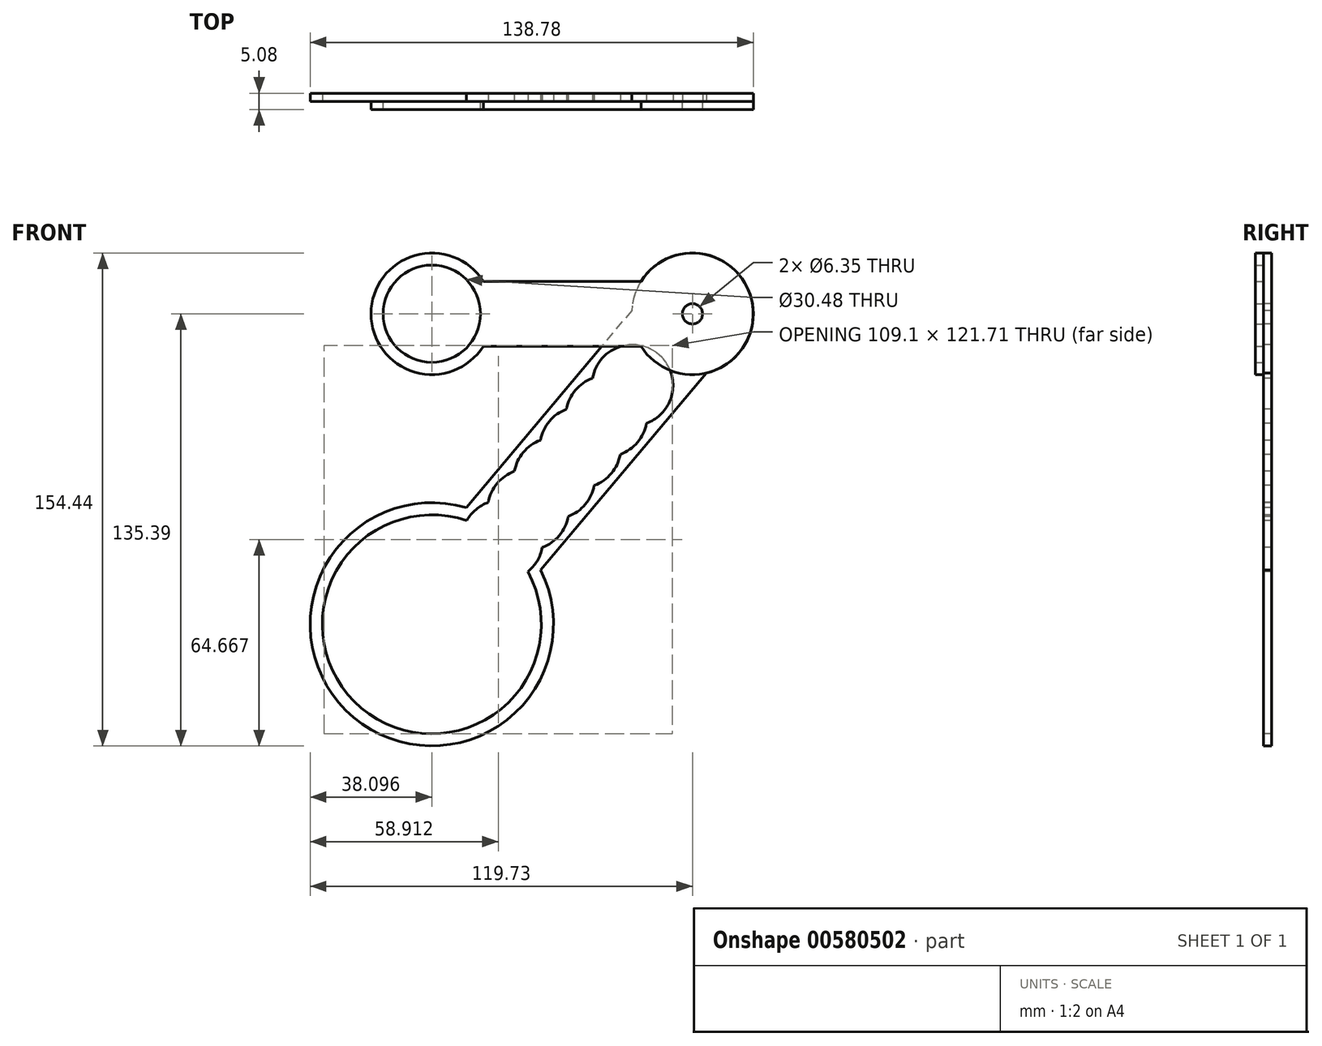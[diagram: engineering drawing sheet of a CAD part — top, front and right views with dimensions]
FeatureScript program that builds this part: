
annotation { "Feature Type Name" : "Feature", "Feature Type Description" : "" }
export const myFeature = defineFeature(function(context is Context, id is Id, definition is map)
    precondition{}
    {
        {
            var Q0;
            Q0=qCreatedBy(makeId("Front.planeOp"),FACE);
            var sketch = newSketch(context, id + "F0", { "sketchPlane" : qUnion([Q0])});
            skCircle(sketch, "E0", {"center": v(-81.63, 0) * mm, "radius": 19.05 * mm});
            skCircle(sketch, "E1", {"center": v(0, 0) * mm, "radius": 19.05 * mm});
            skCircle(sketch, "E2", {"center": v(-81.63, -97.29) * mm, "radius": 38.1 * mm});
            skLineSegment(sketch, "E3", {"start": v(-65.52, 10.16) * mm, "end": v(-16.11, 10.16) * mm});
            skLineSegment(sketch, "E4", {"start": v(4.33, -18.55) * mm, "end": v(-47.51, -80.33) * mm});
            skLineSegment(sketch, "E5", {"start": v(0, 0) * mm, "end": v(-81.63, 0) * mm, "construction": true});
            skLineSegment(sketch, "E6", {"start": v(0, 0) * mm, "end": v(-81.63, -97.29) * mm, "construction": true});
            skLineSegment(sketch, "E7.MirrorCS", {"start": v(-65.52, -10.16) * mm, "end": v(-16.11, -10.16) * mm});
            skLineSegment(sketch, "E8.MirrorCS", {"start": v(-19.02, 1.04) * mm, "end": v(-70.86, -60.74) * mm});
            skCircle(sketch, "E9", {"center": v(0, 0) * mm, "radius": 3.18 * mm});
            skCircle(sketch, "E10", {"center": v(-81.63, 0) * mm, "radius": 15.24 * mm});
            skCircle(sketch, "E11", {"center": v(-81.63, -97.29) * mm, "radius": 34.3 * mm});
            skCircle(sketch, "E12", {"center": v(-59.6, -71.02) * mm, "radius": 12.7 * mm});
            skCircle(sketch, "E13", {"center": v(-51.43, -61.3) * mm, "radius": 12.7 * mm});
            skCircle(sketch, "E14", {"center": v(-43.27, -51.56) * mm, "radius": 12.7 * mm});
            skCircle(sketch, "E15", {"center": v(-35.1, -41.83) * mm, "radius": 12.7 * mm});
            skCircle(sketch, "E16", {"center": v(-26.94, -32.1) * mm, "radius": 12.7 * mm});
            skCircle(sketch, "E17", {"center": v(-18.78, -22.38) * mm, "radius": 12.7 * mm});
            skSolve(sketch);
        }
        {
            var Q0;
            {var subQ0=sQuery(id+"F0.wireOp",EDGE,"E0");var subQ1=makeQuery(id+"F0.imprint","INTERSECT",VERTEX,{"derivedFrom":[subQ0,sQuery(id+"F0.wireOp",EDGE,"E3")]});Q0=makeQuery(id+"F0.imprint","IMPRINT",FACE,{"disambiguationData":[TD([[makeQuery(id+"F0.imprint","IMPRINT",EDGE,{"disambiguationData":[TD([[subQ1,-1.0]])],"derivedFrom":subQ0}),1.0]])]});}
            var Q1;
            {var subQ5=sQuery(id+"F0.wireOp",EDGE,"E3");Q1=makeQuery(id+"F0.imprint","IMPRINT",FACE,{"disambiguationData":[TD([[makeQuery(id+"F0.imprint","IMPRINT",EDGE,{"derivedFrom":subQ5}),-1.0]])]});}
            var Q2;
            {var subQ0=sQuery(id+"F0.wireOp",EDGE,"E1");var subQ1=makeQuery(id+"F0.imprint","INTERSECT",VERTEX,{"derivedFrom":[subQ0,sQuery(id+"F0.wireOp",EDGE,"E3")]});Q2=makeQuery(id+"F0.imprint","IMPRINT",FACE,{"disambiguationData":[TD([[makeQuery(id+"F0.imprint","IMPRINT",EDGE,{"disambiguationData":[TD([[subQ1,-1.0]])],"derivedFrom":subQ0}),1.0]])]});}
            var Q3;
            {var subQ0=sQuery(id+"F0.wireOp",EDGE,"E7.MirrorCS");var subQ1=sQuery(id+"F0.wireOp",EDGE,"E1");var subQ2=makeQuery(id+"F0.imprint","INTERSECT",VERTEX,{"derivedFrom":[subQ1,subQ0]});Q3=makeQuery(id+"F0.imprint","IMPRINT",FACE,{"disambiguationData":[TD([[makeQuery(id+"F0.imprint","IMPRINT",EDGE,{"disambiguationData":[TD([[subQ2,1.0]])],"derivedFrom":subQ1}),-1.0]])]});}
            var Q4;
            {var subQ0=sQuery(id+"F0.wireOp",EDGE,"E8.MirrorCS");var subQ1=sQuery(id+"F0.wireOp",EDGE,"E1");var subQ2=makeQuery(id+"F0.imprint","INTERSECT",VERTEX,{"derivedFrom":[subQ1,subQ0]});Q4=makeQuery(id+"F0.imprint","IMPRINT",FACE,{"disambiguationData":[TD([[makeQuery(id+"F0.imprint","IMPRINT",EDGE,{"disambiguationData":[TD([[subQ2,-1.0]])],"derivedFrom":subQ1}),-1.0]])]});}
            var Q5;
            {var subQ0=sQuery(id+"F0.wireOp",EDGE,"E1");var subQ1=makeQuery(id+"F0.imprint","INTERSECT",VERTEX,{"derivedFrom":[subQ0,sQuery(id+"F0.wireOp",EDGE,"E7.MirrorCS")]});Q5=makeQuery(id+"F0.imprint","IMPRINT",FACE,{"disambiguationData":[TD([[makeQuery(id+"F0.imprint","IMPRINT",EDGE,{"disambiguationData":[TD([[subQ1,1.0]])],"derivedFrom":subQ0}),1.0]])]});}
            extrude(context, id + "F1", {"entities" : qUnion([Q0, Q1, Q2, Q3, Q4, Q5]), "depth" : 2.54 * mm, "offsetDistance" : 25.4 * mm});
        }
        {
            var Q0;
            {var subQ5=sQuery(id+"F0.wireOp",EDGE,"E4");Q0=makeQuery(id+"F0.imprint","IMPRINT",FACE,{"disambiguationData":[TD([[makeQuery(id+"F0.imprint","IMPRINT",EDGE,{"derivedFrom":subQ5}),-1.0]])]});}
            var Q1;
            {var subQ0=sQuery(id+"F0.wireOp",EDGE,"E2");var subQ1=makeQuery(id+"F0.imprint","INTERSECT",VERTEX,{"derivedFrom":[subQ0,sQuery(id+"F0.wireOp",EDGE,"E4")]});Q1=makeQuery(id+"F0.imprint","IMPRINT",FACE,{"disambiguationData":[TD([[makeQuery(id+"F0.imprint","IMPRINT",EDGE,{"disambiguationData":[TD([[subQ1,-1.0]])],"derivedFrom":subQ0}),1.0]])]});}
            var Q2;
            {var subQ0=sQuery(id+"F0.wireOp",EDGE,"E8.MirrorCS");var subQ1=sQuery(id+"F0.wireOp",EDGE,"E2");var subQ2=makeQuery(id+"F0.imprint","INTERSECT",VERTEX,{"derivedFrom":[subQ1,subQ0]});Q2=makeQuery(id+"F0.imprint","IMPRINT",FACE,{"disambiguationData":[TD([[makeQuery(id+"F0.imprint","IMPRINT",EDGE,{"disambiguationData":[TD([[subQ2,1.0]])],"derivedFrom":subQ1}),-1.0]])]});}
            var Q3;
            {var subQ0=sQuery(id+"F0.wireOp",EDGE,"E8.MirrorCS");var subQ1=sQuery(id+"F0.wireOp",EDGE,"E1");var subQ2=makeQuery(id+"F0.imprint","INTERSECT",VERTEX,{"derivedFrom":[subQ1,subQ0]});Q3=makeQuery(id+"F0.imprint","IMPRINT",FACE,{"disambiguationData":[TD([[makeQuery(id+"F0.imprint","IMPRINT",EDGE,{"disambiguationData":[TD([[subQ2,-1.0]])],"derivedFrom":subQ1}),-1.0]])]});}
            var Q4;
            Q4=makeQuery(id+"F0.imprint","IMPRINT",FACE,{"disambiguationData":[TD([[makeQuery(id+"F0.imprint","IMPRINT",EDGE,{"derivedFrom":sQuery(id+"F0.wireOp",EDGE,"E9")}),-1.0]])]});
            extrude(context, id + "F2", {"entities" : qUnion([Q0, Q1, Q2, Q3, Q4]), "oppositeDirection" : true, "depth" : 2.54 * mm, "offsetDistance" : 25.4 * mm});
        }
    });
